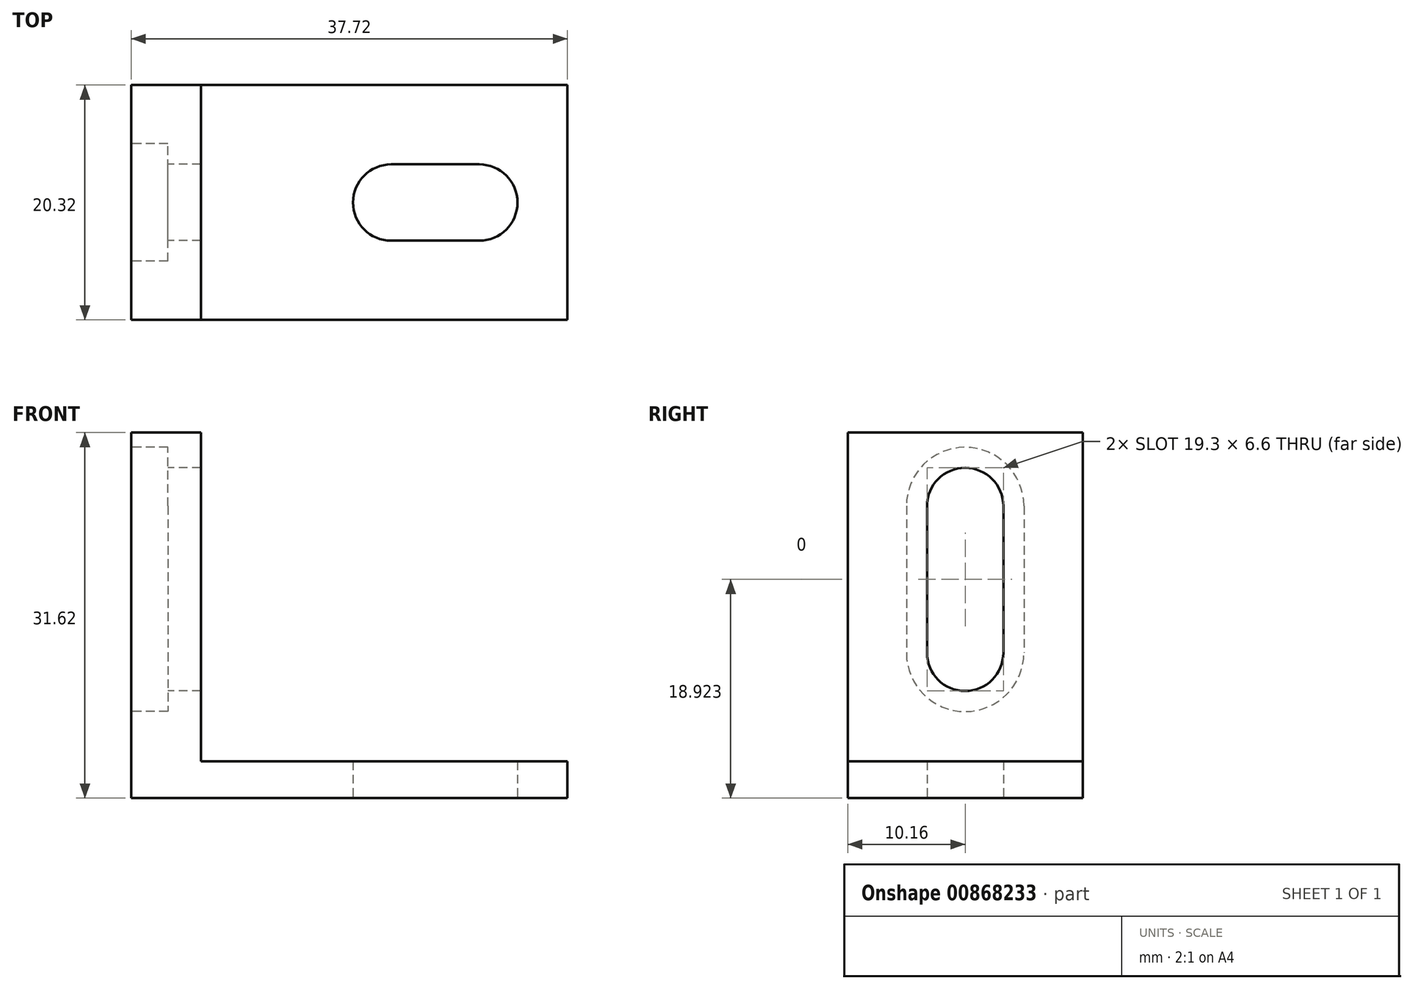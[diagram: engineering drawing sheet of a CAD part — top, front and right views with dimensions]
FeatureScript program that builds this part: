
annotation { "Feature Type Name" : "Feature", "Feature Type Description" : "" }
export const myFeature = defineFeature(function(context is Context, id is Id, definition is map)
    precondition{}
    {
        {
            var Q0;
            Q0=qCreatedBy(makeId("Front.planeOp"),FACE);
            var sketch = newSketch(context, id + "F0", { "sketchPlane" : qUnion([Q0])});
            skLineSegment(sketch, "E0", {"start": v(0, 0) * mm, "end": v(37.72, 0) * mm});
            skLineSegment(sketch, "E1", {"start": v(37.72, 0) * mm, "end": v(37.72, 3.18) * mm});
            skLineSegment(sketch, "E2", {"start": v(37.72, 3.17) * mm, "end": v(6.02, 3.17) * mm});
            skLineSegment(sketch, "E3", {"start": v(6.02, 3.17) * mm, "end": v(6.02, 31.62) * mm});
            skLineSegment(sketch, "E4", {"start": v(6.02, 31.62) * mm, "end": v(0, 31.62) * mm});
            skLineSegment(sketch, "E5", {"start": v(0, 31.62) * mm, "end": v(0, 0) * mm});
            skSolve(sketch);
        }
        {
            var Q0;
            Q0=makeQuery(id+"F0.imprint","IMPRINT",FACE,{"disambiguationData":[TD([[makeQuery(id+"F0.imprint","IMPRINT",EDGE,{"derivedFrom":sQuery(id+"F0.wireOp",EDGE,"E0")}),1.0]])]});
            extrude(context, id + "F1", {"entities" : qUnion([Q0]), "depth" : 20.32 * mm, "offsetDistance" : 25.4 * mm});
        }
        {
            var Q0;
            Q0=makeQuery(id+"F1.opExtrude","SWEPT_FACE",FACE,{"disambiguationData":[OSD([sQuery(id+"F0.wireOp",EDGE,"E0")])]});
            var sketch = newSketch(context, id + "F2", { "sketchPlane" : qUnion([Q0])});
            skArc(sketch, "E6", {"start": v(30.1, 6.86) * mm, "mid": v(33.4, 10.16) * mm, "end": v(30.1, 13.46) * mm});
            skPoint(sketch, "E6.centerSnap0", {"position": v(37.72, 10.16) * mm});
            skArc(sketch, "E7", {"start": v(22.48, 13.46) * mm, "mid": v(19.18, 10.16) * mm, "end": v(22.48, 6.86) * mm});
            skLineSegment(sketch, "E8", {"start": v(22.48, 13.46) * mm, "end": v(30.1, 13.46) * mm});
            skLineSegment(sketch, "E9", {"start": v(30.1, 6.86) * mm, "end": v(22.48, 6.86) * mm});
            skSolve(sketch);
        }
        {
            var Q0;
            Q0=makeQuery(id+"F2.imprint","IMPRINT",FACE,{"disambiguationData":[TD([[makeQuery(id+"F2.imprint","IMPRINT",EDGE,{"derivedFrom":sQuery(id+"F2.wireOp",EDGE,"E6")}),1.0]])]});
            extrude(context, id + "F3", {"entities" : qUnion([Q0]), "operationType" : NewBodyOperationType.REMOVE, "oppositeDirection" : true, "depth" : 15.24 * mm, "offsetDistance" : 25.4 * mm});
        }
        {
            var Q0;
            Q0=makeQuery(id+"F1.opExtrude","SWEPT_FACE",FACE,{"disambiguationData":[OSD([sQuery(id+"F0.wireOp",EDGE,"E5")])]});
            var sketch = newSketch(context, id + "F4", { "sketchPlane" : qUnion([Q0])});
            skArc(sketch, "E10", {"start": v(13.46, 25.27) * mm, "mid": v(10.16, 28.57) * mm, "end": v(6.86, 25.27) * mm});
            skPoint(sketch, "E10.centerSnap0", {"position": v(10.16, 31.62) * mm});
            skArc(sketch, "E11", {"start": v(6.86, 12.57) * mm, "mid": v(10.16, 9.27) * mm, "end": v(13.46, 12.57) * mm});
            skLineSegment(sketch, "E12", {"start": v(6.86, 25.27) * mm, "end": v(6.86, 12.57) * mm});
            skLineSegment(sketch, "E13", {"start": v(13.46, 25.27) * mm, "end": v(13.46, 12.57) * mm});
            skArc(sketch, "E14", {"start": v(15.24, 25.27) * mm, "mid": v(10.16, 30.35) * mm, "end": v(5.08, 25.27) * mm});
            skArc(sketch, "E15", {"start": v(5.08, 12.57) * mm, "mid": v(10.16, 7.5) * mm, "end": v(15.24, 12.57) * mm});
            skLineSegment(sketch, "E16", {"start": v(15.24, 25.27) * mm, "end": v(15.24, 12.57) * mm});
            skLineSegment(sketch, "E17", {"start": v(5.08, 25.27) * mm, "end": v(5.08, 12.57) * mm});
            skSolve(sketch);
        }
        {
            var Q0;
            Q0=makeQuery(id+"F4.imprint","IMPRINT",FACE,{"disambiguationData":[TD([[makeQuery(id+"F4.imprint","IMPRINT",EDGE,{"derivedFrom":sQuery(id+"F4.wireOp",EDGE,"E10")}),1.0]])]});
            extrude(context, id + "F5", {"entities" : qUnion([Q0]), "operationType" : NewBodyOperationType.REMOVE, "oppositeDirection" : true, "depth" : 25.4 * mm, "offsetDistance" : 25.4 * mm});
        }
        {
            var Q0;
            Q0 = qSketchRegion(id + "F4", true);
            extrude(context, id + "F6", {"entities" : qUnion([Q0]), "operationType" : NewBodyOperationType.REMOVE, "oppositeDirection" : true, "depth" : 3.17 * mm, "offsetDistance" : 25.4 * mm});
        }
    });
